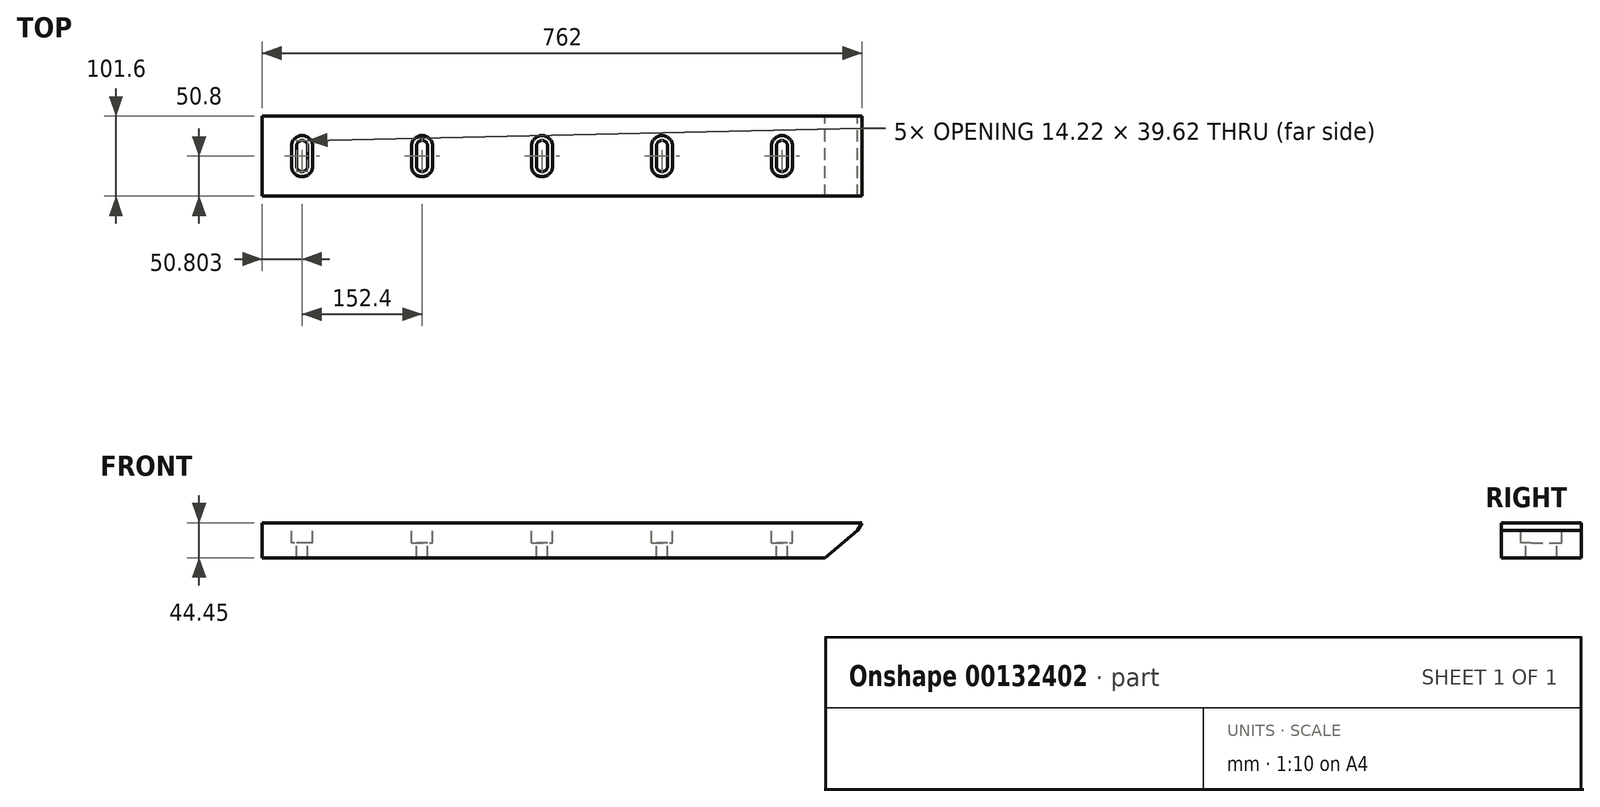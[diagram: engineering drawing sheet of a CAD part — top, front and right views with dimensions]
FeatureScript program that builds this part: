
annotation { "Feature Type Name" : "Feature", "Feature Type Description" : "" }
export const myFeature = defineFeature(function(context is Context, id is Id, definition is map)
    precondition{}
    {
        {
            var Q0;
            Q0=qCreatedBy(makeId("Front.planeOp"),FACE);
            var sketch = newSketch(context, id + "F0", { "sketchPlane" : qUnion([Q0])});
            skLineSegment(sketch, "E0", {"start": v(-347.7, -79.27) * mm, "end": v(-347.7, -34.82) * mm});
            skLineSegment(sketch, "E1", {"start": v(-347.7, -34.82) * mm, "end": v(414.3, -34.82) * mm});
            skLineSegment(sketch, "E2", {"start": v(367.17, -79.27) * mm, "end": v(-347.7, -79.27) * mm});
            skLineSegment(sketch, "E3", {"start": v(414.3, -34.82) * mm, "end": v(408.8, -44.35) * mm});
            skLineSegment(sketch, "E4", {"start": v(408.8, -44.35) * mm, "end": v(367.17, -79.27) * mm});
            skSolve(sketch);
        }
        {
            var Q0;
            Q0=makeQuery(id+"F0.imprint","IMPRINT",FACE,{"disambiguationData":[TD([[makeQuery(id+"F0.imprint","IMPRINT",EDGE,{"derivedFrom":sQuery(id+"F0.wireOp",EDGE,"E0")}),-1.0]])]});
            extrude(context, id + "F1", {"entities" : qUnion([Q0]), "endBound" : BoundingType.SYMMETRIC, "depth" : 101.6 * mm});
        }
        {
            var Q0;
            Q0=makeQuery(id+"F1.opExtrude","SWEPT_FACE",FACE,{"disambiguationData":[OSD([sQuery(id+"F0.wireOp",EDGE,"E1")])]});
            var sketch = newSketch(context, id + "F2", { "sketchPlane" : qUnion([Q0])});
            skLineSegment(sketch, "E5.0", {"start": v(-289.8, -12.7) * mm, "end": v(-289.8, 12.7) * mm});
            skLineSegment(sketch, "E6.0", {"start": v(-304.02, -12.7) * mm, "end": v(-304.02, 12.7) * mm});
            skArc(sketch, "E7", {"start": v(-304.02, 12.7) * mm, "mid": v(-296.9, 19.81) * mm, "end": v(-289.8, 12.7) * mm});
            skArc(sketch, "E8", {"start": v(-304.02, -12.7) * mm, "mid": v(-296.9, -19.81) * mm, "end": v(-289.8, -12.7) * mm});
            skArc(sketch, "E9.0", {"start": v(-310.37, 12.7) * mm, "mid": v(-296.9, 26.16) * mm, "end": v(-283.44, 12.7) * mm});
            skLineSegment(sketch, "E10.0", {"start": v(-283.44, -12.7) * mm, "end": v(-283.44, 12.7) * mm});
            skArc(sketch, "E11.0", {"start": v(-310.37, -12.7) * mm, "mid": v(-296.9, -26.16) * mm, "end": v(-283.44, -12.7) * mm});
            skLineSegment(sketch, "E12.0", {"start": v(-310.37, -12.7) * mm, "end": v(-310.37, 12.7) * mm});
            skArc(sketch, "E13.1.0.0", {"start": v(-157.97, -12.7) * mm, "mid": v(-144.5, -26.16) * mm, "end": v(-131.04, -12.7) * mm});
            skArc(sketch, "E13.1.0.1", {"start": v(-157.97, 12.7) * mm, "mid": v(-144.5, 26.16) * mm, "end": v(-131.04, 12.7) * mm});
            skLineSegment(sketch, "E13.1.0.2", {"start": v(-137.4, -12.7) * mm, "end": v(-137.4, 12.7) * mm});
            skLineSegment(sketch, "E13.1.0.4", {"start": v(-151.62, -12.7) * mm, "end": v(-151.62, 12.7) * mm});
            skArc(sketch, "E13.1.0.5", {"start": v(-151.62, 12.7) * mm, "mid": v(-144.5, 19.81) * mm, "end": v(-137.4, 12.7) * mm});
            skArc(sketch, "E13.1.0.6", {"start": v(-151.62, -12.7) * mm, "mid": v(-144.5, -19.81) * mm, "end": v(-137.4, -12.7) * mm});
            skLineSegment(sketch, "E13.1.0.7", {"start": v(-131.04, -12.7) * mm, "end": v(-131.04, 12.7) * mm});
            skLineSegment(sketch, "E13.1.0.8", {"start": v(-157.97, -12.7) * mm, "end": v(-157.97, 12.7) * mm});
            skArc(sketch, "E13.2.0.0", {"start": v(-5.57, -12.7) * mm, "mid": v(7.9, -26.16) * mm, "end": v(21.36, -12.7) * mm});
            skArc(sketch, "E13.2.0.1", {"start": v(-5.57, 12.7) * mm, "mid": v(7.9, 26.16) * mm, "end": v(21.36, 12.7) * mm});
            skLineSegment(sketch, "E13.2.0.2", {"start": v(15, -12.7) * mm, "end": v(15, 12.7) * mm});
            skLineSegment(sketch, "E13.2.0.4", {"start": v(0.78, -12.7) * mm, "end": v(0.78, 12.7) * mm});
            skArc(sketch, "E13.2.0.5", {"start": v(0.78, 12.7) * mm, "mid": v(7.9, 19.81) * mm, "end": v(15, 12.7) * mm});
            skArc(sketch, "E13.2.0.6", {"start": v(0.78, -12.7) * mm, "mid": v(7.9, -19.81) * mm, "end": v(15, -12.7) * mm});
            skLineSegment(sketch, "E13.2.0.7", {"start": v(21.36, -12.7) * mm, "end": v(21.36, 12.7) * mm});
            skLineSegment(sketch, "E13.2.0.8", {"start": v(-5.57, -12.7) * mm, "end": v(-5.57, 12.7) * mm});
            skArc(sketch, "E13.3.0.0", {"start": v(146.83, -12.7) * mm, "mid": v(160.3, -26.16) * mm, "end": v(173.76, -12.7) * mm});
            skArc(sketch, "E13.3.0.1", {"start": v(146.83, 12.7) * mm, "mid": v(160.3, 26.16) * mm, "end": v(173.76, 12.7) * mm});
            skLineSegment(sketch, "E13.3.0.2", {"start": v(167.4, -12.7) * mm, "end": v(167.4, 12.7) * mm});
            skLineSegment(sketch, "E13.3.0.4", {"start": v(153.18, -12.7) * mm, "end": v(153.18, 12.7) * mm});
            skArc(sketch, "E13.3.0.5", {"start": v(153.18, 12.7) * mm, "mid": v(160.3, 19.81) * mm, "end": v(167.4, 12.7) * mm});
            skArc(sketch, "E13.3.0.6", {"start": v(153.18, -12.7) * mm, "mid": v(160.3, -19.81) * mm, "end": v(167.4, -12.7) * mm});
            skLineSegment(sketch, "E13.3.0.7", {"start": v(173.76, -12.7) * mm, "end": v(173.76, 12.7) * mm});
            skLineSegment(sketch, "E13.3.0.8", {"start": v(146.83, -12.7) * mm, "end": v(146.83, 12.7) * mm});
            skArc(sketch, "E13.4.0.0", {"start": v(299.23, -12.7) * mm, "mid": v(312.7, -26.16) * mm, "end": v(326.16, -12.7) * mm});
            skArc(sketch, "E13.4.0.1", {"start": v(299.23, 12.7) * mm, "mid": v(312.7, 26.16) * mm, "end": v(326.16, 12.7) * mm});
            skLineSegment(sketch, "E13.4.0.2", {"start": v(319.8, -12.7) * mm, "end": v(319.8, 12.7) * mm});
            skLineSegment(sketch, "E13.4.0.4", {"start": v(305.58, -12.7) * mm, "end": v(305.58, 12.7) * mm});
            skArc(sketch, "E13.4.0.5", {"start": v(305.58, 12.7) * mm, "mid": v(312.7, 19.81) * mm, "end": v(319.8, 12.7) * mm});
            skArc(sketch, "E13.4.0.6", {"start": v(305.58, -12.7) * mm, "mid": v(312.7, -19.81) * mm, "end": v(319.8, -12.7) * mm});
            skLineSegment(sketch, "E13.4.0.7", {"start": v(326.16, -12.7) * mm, "end": v(326.16, 12.7) * mm});
            skLineSegment(sketch, "E13.4.0.8", {"start": v(299.23, -12.7) * mm, "end": v(299.23, 12.7) * mm});
            skLineSegment(sketch, "E13.direction1", {"start": v(-310.37, -12.7) * mm, "end": v(-157.97, -12.7) * mm, "construction": true});
            skSolve(sketch);
        }
        {
            var Q0;
            Q0=makeQuery(id+"F2.imprint","IMPRINT",FACE,{"disambiguationData":[TD([[makeQuery(id+"F2.imprint","IMPRINT",EDGE,{"derivedFrom":sQuery(id+"F2.wireOp",EDGE,"E5.0")}),1.0]])]});
            var Q1;
            Q1=makeQuery(id+"F2.imprint","IMPRINT",FACE,{"disambiguationData":[TD([[makeQuery(id+"F2.imprint","IMPRINT",EDGE,{"derivedFrom":sQuery(id+"F2.wireOp",EDGE,"E13.1.0.2")}),1.0]])]});
            var Q2;
            Q2=makeQuery(id+"F2.imprint","IMPRINT",FACE,{"disambiguationData":[TD([[makeQuery(id+"F2.imprint","IMPRINT",EDGE,{"derivedFrom":sQuery(id+"F2.wireOp",EDGE,"E13.2.0.2")}),1.0]])]});
            var Q3;
            Q3=makeQuery(id+"F2.imprint","IMPRINT",FACE,{"disambiguationData":[TD([[makeQuery(id+"F2.imprint","IMPRINT",EDGE,{"derivedFrom":sQuery(id+"F2.wireOp",EDGE,"E13.3.0.2")}),1.0]])]});
            var Q4;
            Q4=makeQuery(id+"F2.imprint","IMPRINT",FACE,{"disambiguationData":[TD([[makeQuery(id+"F2.imprint","IMPRINT",EDGE,{"derivedFrom":sQuery(id+"F2.wireOp",EDGE,"E13.4.0.2")}),1.0]])]});
            extrude(context, id + "F3", {"entities" : qUnion([Q0, Q1, Q2, Q3, Q4]), "operationType" : NewBodyOperationType.REMOVE, "endBound" : BoundingType.THROUGH_ALL, "oppositeDirection" : true, "depth" : 25.4 * mm});
        }
        {
            var Q0;
            Q0=makeQuery(id+"F2.imprint","IMPRINT",FACE,{"disambiguationData":[TD([[makeQuery(id+"F2.imprint","IMPRINT",EDGE,{"derivedFrom":sQuery(id+"F2.wireOp",EDGE,"E5.0")}),-1.0]])]});
            var Q1;
            Q1=makeQuery(id+"F2.imprint","IMPRINT",FACE,{"disambiguationData":[TD([[makeQuery(id+"F2.imprint","IMPRINT",EDGE,{"derivedFrom":sQuery(id+"F2.wireOp",EDGE,"E13.1.0.0")}),1.0]])]});
            var Q2;
            Q2=makeQuery(id+"F2.imprint","IMPRINT",FACE,{"disambiguationData":[TD([[makeQuery(id+"F2.imprint","IMPRINT",EDGE,{"derivedFrom":sQuery(id+"F2.wireOp",EDGE,"E13.2.0.0")}),1.0]])]});
            var Q3;
            Q3=makeQuery(id+"F2.imprint","IMPRINT",FACE,{"disambiguationData":[TD([[makeQuery(id+"F2.imprint","IMPRINT",EDGE,{"derivedFrom":sQuery(id+"F2.wireOp",EDGE,"E13.3.0.0")}),1.0]])]});
            var Q4;
            Q4=makeQuery(id+"F2.imprint","IMPRINT",FACE,{"disambiguationData":[TD([[makeQuery(id+"F2.imprint","IMPRINT",EDGE,{"derivedFrom":sQuery(id+"F2.wireOp",EDGE,"E13.4.0.0")}),1.0]])]});
            extrude(context, id + "F4", {"entities" : qUnion([Q0, Q1, Q2, Q3, Q4]), "operationType" : NewBodyOperationType.REMOVE, "oppositeDirection" : true, "depth" : 25.4 * mm});
        }
    });
